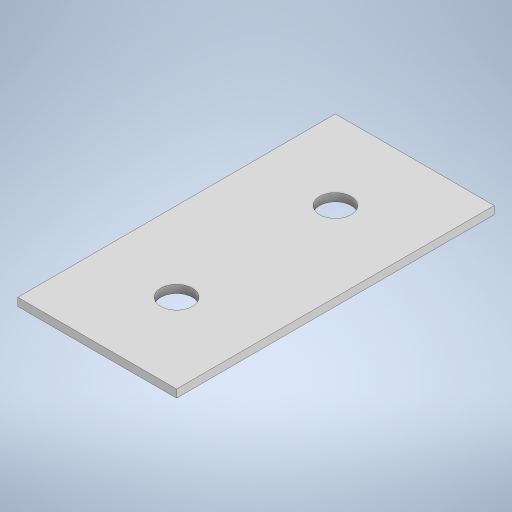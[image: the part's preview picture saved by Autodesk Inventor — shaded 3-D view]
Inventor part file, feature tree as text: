
AUTODESK INVENTOR PART (.ipt)
format: ipt  version: 2023 (Build 270158000, 158)  size: 216,064 bytes
history: native  units: mm
features: other x1, extrude x1, sketch x1
ambient origin geometry x8: Origin, YZ Plane, XZ Plane, XY Plane, X Axis, Y Axis, Z Axis, Center Point
bodies: Body1 (feature_tree)
feature tree (3):
  other  "Твердое тело1"
  extrude  "Выдавливание1"  Depth=40.0mm
  sketch  "Эскиз1"
